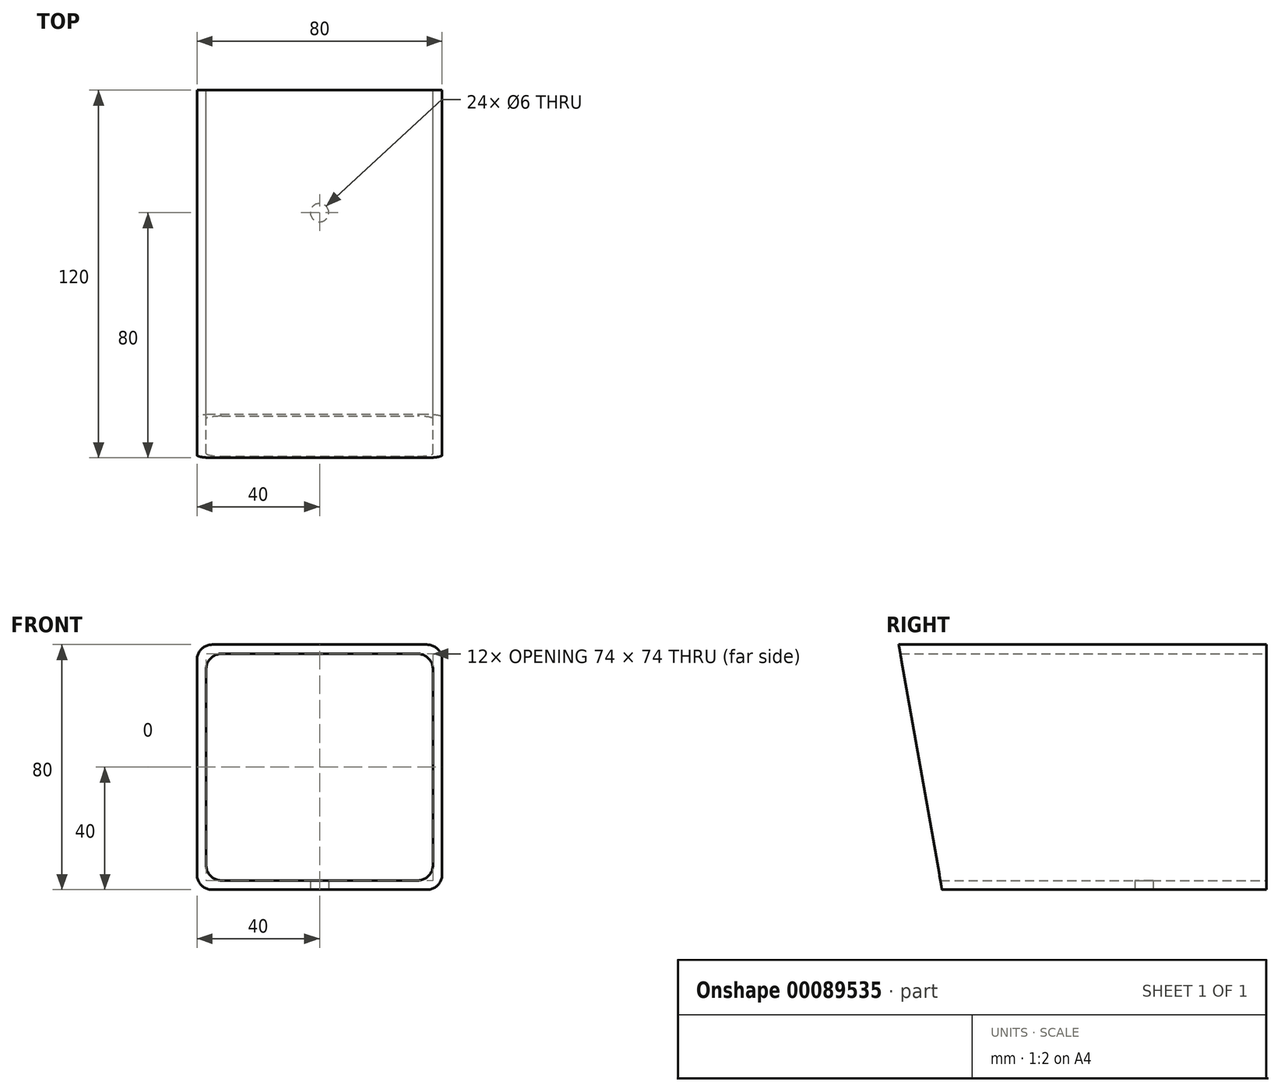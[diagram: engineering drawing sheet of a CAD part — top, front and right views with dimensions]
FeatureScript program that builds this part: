
annotation { "Feature Type Name" : "Feature", "Feature Type Description" : "" }
export const myFeature = defineFeature(function(context is Context, id is Id, definition is map)
    precondition{}
    {
        {
            var Q0;
            Q0=qCreatedBy(makeId("Front.planeOp"),FACE);
            var sketch = newSketch(context, id + "F0", { "sketchPlane" : qUnion([Q0])});
            skLineSegment(sketch, "E0.bottom", {"start": v(40, -40) * mm, "end": v(-40, -40) * mm});
            skLineSegment(sketch, "E0.top", {"start": v(40, 40) * mm, "end": v(-40, 40) * mm});
            skLineSegment(sketch, "E0.left", {"start": v(40, -40) * mm, "end": v(40, 40) * mm});
            skLineSegment(sketch, "E0.right", {"start": v(-40, -40) * mm, "end": v(-40, 40) * mm});
            skPoint(sketch, "E0.middle", {"position": v(0, 0) * mm});
            skLineSegment(sketch, "E1.0", {"start": v(37, 37) * mm, "end": v(-37, 37) * mm});
            skLineSegment(sketch, "E1.1", {"start": v(37, -37) * mm, "end": v(37, 37) * mm});
            skLineSegment(sketch, "E1.2", {"start": v(37, -37) * mm, "end": v(-37, -37) * mm});
            skLineSegment(sketch, "E1.3", {"start": v(-37, -37) * mm, "end": v(-37, 37) * mm});
            skSolve(sketch);
        }
        {
            var Q0;
            Q0=makeQuery(id+"F0.imprint","IMPRINT",FACE,{"disambiguationData":[TD([[makeQuery(id+"F0.imprint","IMPRINT",EDGE,{"derivedFrom":sQuery(id+"F0.wireOp",EDGE,"E0.bottom")}),-1.0]])]});
            extrude(context, id + "F1", {"entities" : qUnion([Q0]), "depth" : 120 * mm});
        }
        {
            var Q0;
            Q0=makeQuery(id+"F1.opExtrude","SWEPT_FACE",FACE,{"disambiguationData":[OSD([sQuery(id+"F0.wireOp",EDGE,"E0.right")])]});
            var sketch = newSketch(context, id + "F2", { "sketchPlane" : qUnion([Q0])});
            skLineSegment(sketch, "E2", {"start": v(120, 40) * mm, "end": v(105.9, -40) * mm});
            skSolve(sketch);
        }
        {
            var Q0;
            {var subQ0=sQuery(id+"F2.wireOp",EDGE,"E2");Q0=makeQuery(id+"F2.imprint","IMPRINT",FACE,{"disambiguationData":[TD([[makeQuery(id+"F2.imprint","IMPRINT",EDGE,{"derivedFrom":subQ0}),1.0]])]});}
            extrude(context, id + "F3", {"entities" : qUnion([Q0]), "operationType" : NewBodyOperationType.REMOVE, "endBound" : BoundingType.THROUGH_ALL, "oppositeDirection" : true, "depth" : 25 * mm});
        }
        {
            var Q0;
            Q0=makeQuery(id+"F1.opExtrude","SWEPT_FACE",FACE,{"disambiguationData":[OSD([sQuery(id+"F0.wireOp",EDGE,"E0.bottom")])]});
            var sketch = newSketch(context, id + "F4", { "sketchPlane" : qUnion([Q0])});
            skLineSegment(sketch, "E3", {"start": v(0, 0) * mm, "end": v(0, 105.9) * mm, "construction": true});
            skLineSegment(sketch, "E4", {"start": v(-40, 40) * mm, "end": v(40, 40) * mm, "construction": true});
            skCircle(sketch, "E5", {"center": v(0, 40) * mm, "radius": 3 * mm});
            skSolve(sketch);
        }
        {
            var Q0;
            {var subQ0=sQuery(id+"F4.wireOp",EDGE,"XbUR5iSa-2E6P-xa2R-k8sD-Wkvi0jSxQQ6j");var subQ1=sQuery(id+"F4.wireOp",EDGE,"j9we0SoD-WnQy-cOkZ-ErFc-ImfEjKtu8c7R");var subQ2=makeQuery(id+"F4.imprint","INTERSECT",VERTEX,{"derivedFrom":[subQ1,subQ0]});Q0=makeQuery(id+"F4.imprint","IMPRINT",FACE,{"disambiguationData":[TD([[makeQuery(id+"F4.imprint","IMPRINT",EDGE,{"disambiguationData":[TD([[subQ2,1.0]])],"derivedFrom":subQ1}),1.0]])]});}
            var Q1;
            {var subQ0=sQuery(id+"F4.wireOp",EDGE,"0MyaLaYq-l7yQ-eMNX-CSdv-fVzSeGhlYCIf");Q1=makeQuery(id+"F4.imprint","IMPRINT",FACE,{"disambiguationData":[TD([[makeQuery(id+"F4.imprint","IMPRINT",EDGE,{"derivedFrom":subQ0}),-1.0]])]});}
            var Q2;
            Q2=makeQuery(id+"F4.imprint","IMPRINT",FACE,{"disambiguationData":[TD([[makeQuery(id+"F4.imprint","IMPRINT",EDGE,{"derivedFrom":sQuery(id+"F4.wireOp",EDGE,"E5")}),1.0]])]});
            extrude(context, id + "F5", {"entities" : qUnion([Q0, Q1, Q2]), "operationType" : NewBodyOperationType.REMOVE, "oppositeDirection" : true, "depth" : 25 * mm});
        }
        {
            var Q0;
            Q0=makeQuery(id+"F1.opExtrude","SWEPT_EDGE",EDGE,{"disambiguationData":[OSD([sQuery(id+"F0.wireOp",EDGE,"E0.top"),sQuery(id+"F0.wireOp",EDGE,"E0.left")])]});
            var Q1;
            Q1=makeQuery(id+"F1.opExtrude","SWEPT_EDGE",EDGE,{"disambiguationData":[OSD([sQuery(id+"F0.wireOp",EDGE,"E0.bottom"),sQuery(id+"F0.wireOp",EDGE,"E0.left")])]});
            var Q2;
            Q2=makeQuery(id+"F1.opExtrude","SWEPT_EDGE",EDGE,{"disambiguationData":[OSD([sQuery(id+"F0.wireOp",EDGE,"E0.top"),sQuery(id+"F0.wireOp",EDGE,"E0.right")])]});
            var Q3;
            Q3=makeQuery(id+"F1.opExtrude","SWEPT_EDGE",EDGE,{"disambiguationData":[OSD([sQuery(id+"F0.wireOp",EDGE,"E0.bottom"),sQuery(id+"F0.wireOp",EDGE,"E0.right")])]});
            var Q4;
            Q4=makeQuery(id+"F1.opExtrude","SWEPT_EDGE",EDGE,{"disambiguationData":[OSD([sQuery(id+"F0.wireOp",EDGE,"E1.0"),sQuery(id+"F0.wireOp",EDGE,"E1.1")])]});
            var Q5;
            Q5=makeQuery(id+"F1.opExtrude","SWEPT_EDGE",EDGE,{"disambiguationData":[OSD([sQuery(id+"F0.wireOp",EDGE,"E1.1"),sQuery(id+"F0.wireOp",EDGE,"E1.2")])]});
            var Q6;
            Q6=makeQuery(id+"F1.opExtrude","SWEPT_EDGE",EDGE,{"disambiguationData":[OSD([sQuery(id+"F0.wireOp",EDGE,"E1.2"),sQuery(id+"F0.wireOp",EDGE,"E1.3")])]});
            var Q7;
            Q7=makeQuery(id+"F1.opExtrude","SWEPT_EDGE",EDGE,{"disambiguationData":[OSD([sQuery(id+"F0.wireOp",EDGE,"E1.0"),sQuery(id+"F0.wireOp",EDGE,"E1.3")])]});
            fillet(context, id + "F6", {"entities" : qUnion([Q0, Q1, Q2, Q3, Q4, Q5, Q6, Q7]), "radius" : 5 * mm, "tangentPropagation" : true, "allowEdgeOverflow" : false});
        }
    });
